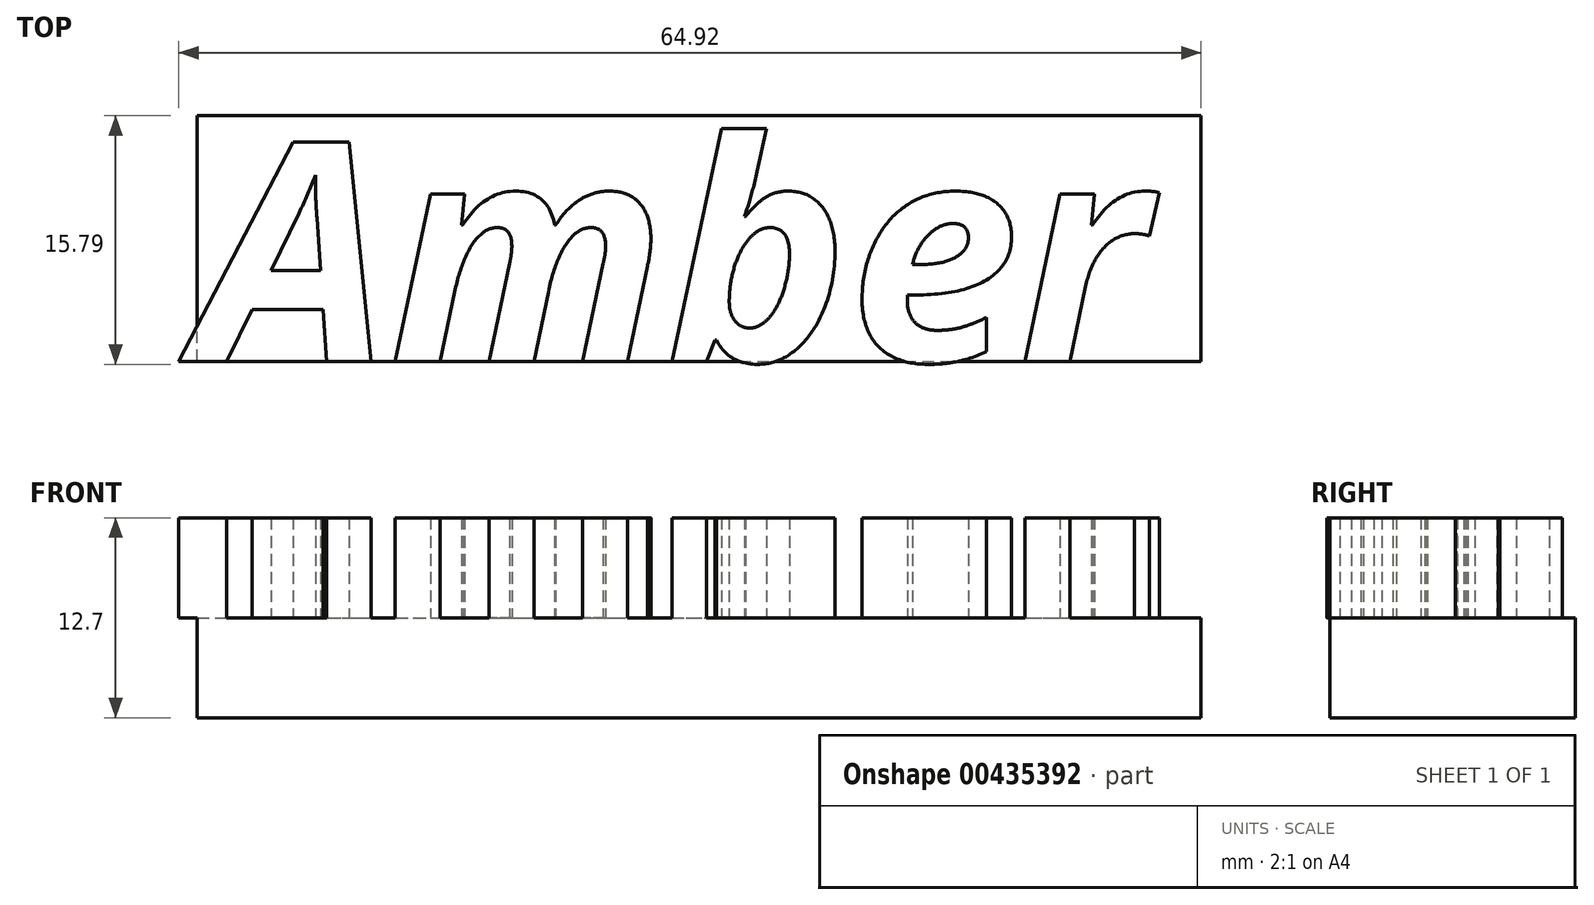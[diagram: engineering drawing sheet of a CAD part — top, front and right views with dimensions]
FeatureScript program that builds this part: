
annotation { "Feature Type Name" : "Feature", "Feature Type Description" : "" }
export const myFeature = defineFeature(function(context is Context, id is Id, definition is map)
    precondition{}
    {
        {
            var Q0;
            Q0=qCreatedBy(makeId("Top.planeOp"),FACE);
            var sketch = newSketch(context, id + "F0", { "sketchPlane" : qUnion([Q0])});
            skText(sketch, "E0", { "text": "Amber", "fontName": "OpenSans-BoldItalic.ttf"});
            const initialGuessF0  = {"E0": [0, 0, 1, 0, 0.014]};
            skSetInitialGuess(sketch, initialGuessF0);
            skSolve(sketch);
        }
        {
            var Q0;
            Q0=qCreatedBy(makeId("Top.planeOp"),FACE);
            var sketch = newSketch(context, id + "F1", { "sketchPlane" : qUnion([Q0])});
            skLineSegment(sketch, "E1", {"start": v(-0.29, 16.12) * mm, "end": v(63.9, 16.12) * mm});
            skLineSegment(sketch, "E2", {"start": v(63.9, 16.12) * mm, "end": v(63.9, 0) * mm});
            skSolve(sketch);
        }
        {
            var Q0;
            Q0=qCreatedBy(makeId("Top.planeOp"),FACE);
            var sketch = newSketch(context, id + "F2", { "sketchPlane" : qUnion([Q0])});
            skLineSegment(sketch, "E3.bottom", {"start": v(0, 0) * mm, "end": v(63.75, 0) * mm});
            skLineSegment(sketch, "E3.top", {"start": v(0, 15.6) * mm, "end": v(63.75, 15.6) * mm});
            skLineSegment(sketch, "E3.left", {"start": v(0, 0) * mm, "end": v(0, 15.6) * mm});
            skLineSegment(sketch, "E3.right", {"start": v(63.75, 0) * mm, "end": v(63.75, 15.6) * mm});
            skSolve(sketch);
        }
        {
            var Q0;
            Q0 = qSketchRegion(id + "F2", true);
            extrude(context, id + "F3", {"entities" : qUnion([Q0]), "oppositeDirection" : true, "depth" : 6.35 * mm});
        }
        {
            var Q0;
            Q0 = qSketchRegion(id + "F1", true);
            var Q1;
            Q1 = qSketchRegion(id + "F0", true);
            extrude(context, id + "F4", {"entities" : qUnion([Q0, Q1]), "operationType" : NewBodyOperationType.ADD, "depth" : 6.35 * mm});
        }
    });
